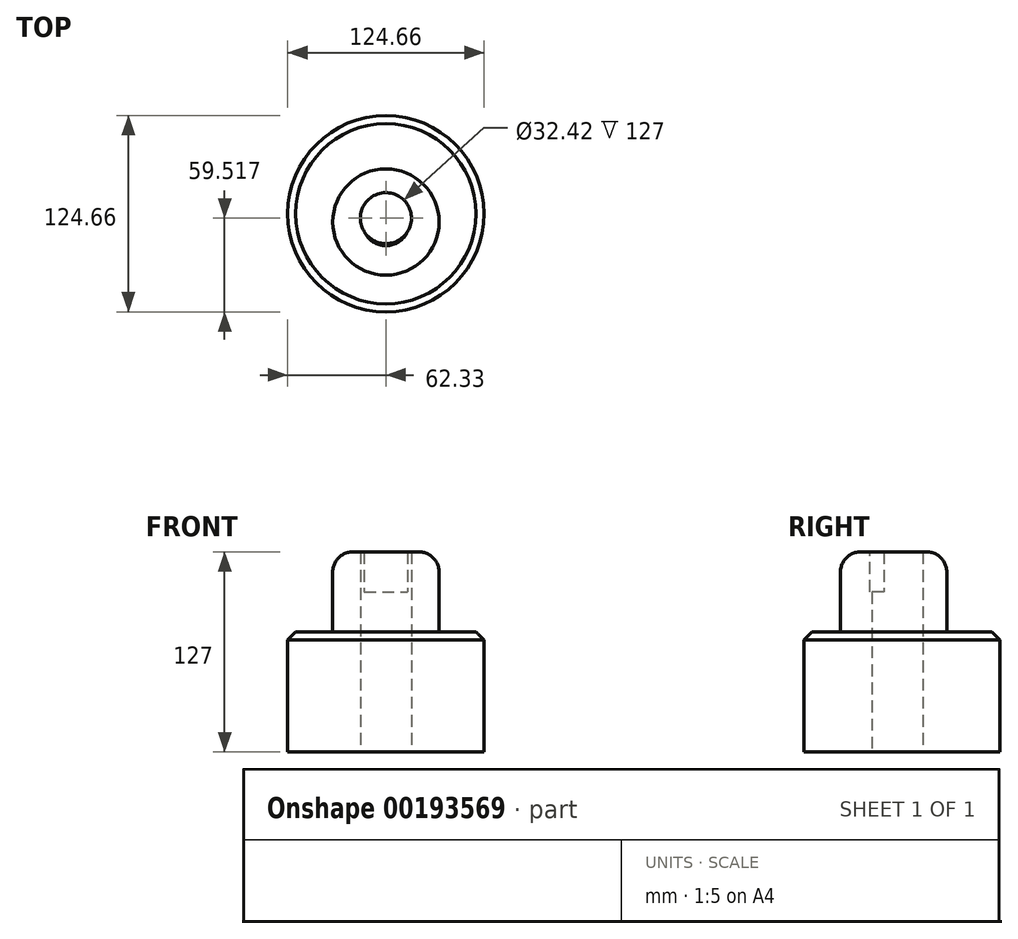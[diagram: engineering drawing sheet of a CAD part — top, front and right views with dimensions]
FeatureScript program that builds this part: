
annotation { "Feature Type Name" : "Feature", "Feature Type Description" : "" }
export const myFeature = defineFeature(function(context is Context, id is Id, definition is map)
    precondition{}
    {
        {
            var Q0;
            Q0=qCreatedBy(makeId("Top.planeOp"),FACE);
            var sketch = newSketch(context, id + "F0", { "sketchPlane" : qUnion([Q0])});
            skCircle(sketch, "E0", {"center": v(0, 5.26) * mm, "radius": 62.33 * mm});
            skSolve(sketch);
        }
        {
            var Q0;
            Q0=makeQuery(id+"F0.imprint","IMPRINT",FACE,{"disambiguationData":[TD([[makeQuery(id+"F0.imprint","IMPRINT",EDGE,{"derivedFrom":sQuery(id+"F0.wireOp",EDGE,"E0")}),1.0]])]});
            extrude(context, id + "F1", {"entities" : qUnion([Q0]), "depth" : 76.2 * mm});
        }
        {
            var Q0;
            Q0=makeQuery(id+"F1.opExtrude","CAP_FACE",FACE,{"disambiguationData":[OSD([sQuery(id+"F0.wireOp",EDGE,"E0")])],"isStart":false});
            var sketch = newSketch(context, id + "F2", { "sketchPlane" : qUnion([Q0])});
            skCircle(sketch, "E1", {"center": v(0, 0) * mm, "radius": 33.76 * mm});
            skSolve(sketch);
        }
        {
            var Q0;
            Q0 = qSketchRegion(id + "F2", true);
            extrude(context, id + "F3", {"entities" : qUnion([Q0]), "operationType" : NewBodyOperationType.ADD, "depth" : 50.8 * mm});
        }
        {
            var Q0;
            Q0=makeQuery(id+"F3.opExtrude","CAP_FACE",FACE,{"disambiguationData":[OSD([sQuery(id+"F2.wireOp",EDGE,"E1")])],"isStart":false});
            var sketch = newSketch(context, id + "F4", { "sketchPlane" : qUnion([Q0])});
            skCircle(sketch, "E2", {"center": v(0, 0) * mm, "radius": 15.05 * mm});
            skSolve(sketch);
        }
        {
            var Q0;
            Q0=makeQuery(id+"F4.imprint","IMPRINT",FACE,{"disambiguationData":[TD([[makeQuery(id+"F4.imprint","IMPRINT",EDGE,{"derivedFrom":sQuery(id+"F4.wireOp",EDGE,"E2")}),1.0]])]});
            extrude(context, id + "F5", {"entities" : qUnion([Q0]), "operationType" : NewBodyOperationType.REMOVE, "oppositeDirection" : true, "depth" : 25.4 * mm});
        }
        {
            var Q0;
            Q0=makeQuery(id+"F1.opExtrude","CAP_FACE",FACE,{"disambiguationData":[OSD([sQuery(id+"F0.wireOp",EDGE,"E0")])],"isStart":true});
            var sketch = newSketch(context, id + "F6", { "sketchPlane" : qUnion([Q0])});
            skCircle(sketch, "E3", {"center": v(0, -2.45) * mm, "radius": 16.2 * mm});
            skSolve(sketch);
        }
        {
            var Q0;
            Q0=makeQuery(id+"F6.imprint","IMPRINT",FACE,{"disambiguationData":[TD([[makeQuery(id+"F6.imprint","IMPRINT",EDGE,{"derivedFrom":sQuery(id+"F6.wireOp",EDGE,"E3")}),1.0]])]});
            extrude(context, id + "F7", {"entities" : qUnion([Q0]), "operationType" : NewBodyOperationType.REMOVE, "oppositeDirection" : true, "depth" : 25.4 * mm});
        }
        {
            var Q0;
            Q0=makeQuery(id+"F7.boolean.opBoolean","COPY",FACE,{"derivedFrom":makeQuery(id+"F7.opExtrude","CAP_FACE",FACE,{"disambiguationData":[OSD([sQuery(id+"F6.wireOp",EDGE,"E3")])],"isStart":false})});
            extrude(context, id + "F8", {"entities" : qUnion([Q0]), "operationType" : NewBodyOperationType.REMOVE, "oppositeDirection" : true, "depth" : 254 * mm});
        }
        {
            var Q0;
            Q0=makeQuery(id+"F3.opExtrude","CAP_EDGE",EDGE,{"disambiguationData":[OSD([sQuery(id+"F2.wireOp",EDGE,"E1")])],"isStart":false});
            fillet(context, id + "F9", {"entities" : qUnion([Q0]), "radius" : 12.7 * mm, "tangentPropagation" : true, "allowEdgeOverflow" : false});
        }
        {
            var Q0;
            Q0=makeQuery(id+"F1.opExtrude","CAP_EDGE",EDGE,{"disambiguationData":[OSD([sQuery(id+"F0.wireOp",EDGE,"E0")])],"isStart":false});
            chamfer(context, id + "F10", {"entities" : qUnion([Q0]), "width" : 5.08 * mm, "tangentPropagation" : true});
        }
    });
